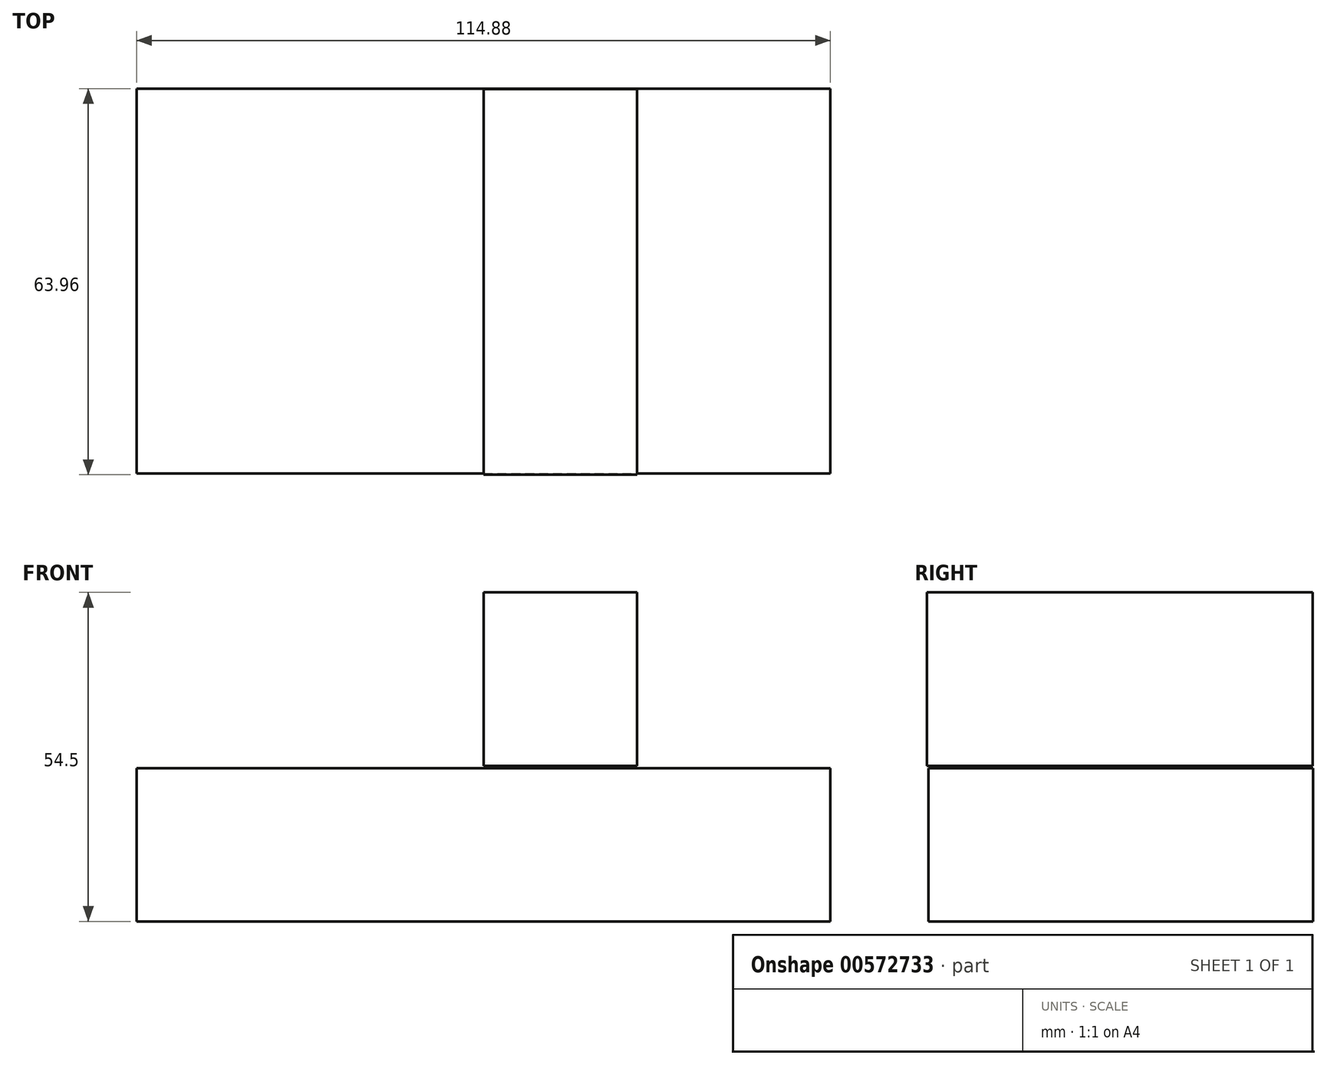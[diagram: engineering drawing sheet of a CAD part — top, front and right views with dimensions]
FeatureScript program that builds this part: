
annotation { "Feature Type Name" : "Feature", "Feature Type Description" : "" }
export const myFeature = defineFeature(function(context is Context, id is Id, definition is map)
    precondition{}
    {
        {
            var Q0;
            Q0=qCreatedBy(makeId("Top.planeOp"),FACE);
            var sketch = newSketch(context, id + "F0", { "sketchPlane" : qUnion([Q0])});
            skLineSegment(sketch, "E0.bottom", {"start": v(-57.44, -31.87) * mm, "end": v(57.44, -31.87) * mm});
            skLineSegment(sketch, "E0.top", {"start": v(-57.44, 31.87) * mm, "end": v(57.44, 31.87) * mm});
            skLineSegment(sketch, "E0.left", {"start": v(-57.44, -31.87) * mm, "end": v(-57.44, 31.87) * mm});
            skLineSegment(sketch, "E0.right", {"start": v(57.44, -31.87) * mm, "end": v(57.44, 31.87) * mm});
            skPoint(sketch, "E0.middle", {"position": v(0, 0) * mm});
            skSolve(sketch);
        }
        {
            var Q0;
            Q0 = qSketchRegion(id + "F0", true);
            extrude(context, id + "F1", {"entities" : qUnion([Q0]), "depth" : 25.4 * mm, "offsetDistance" : 25.4 * mm});
        }
        {
            var Q0;
            Q0=qCreatedBy(makeId("Right.planeOp"),FACE);
            var sketch = newSketch(context, id + "F2", { "sketchPlane" : qUnion([Q0])});
            skLineSegment(sketch, "E1.bottom", {"start": v(31.8, 54.5) * mm, "end": v(-32.09, 54.5) * mm});
            skLineSegment(sketch, "E1.top", {"start": v(31.8, 25.78) * mm, "end": v(-32.09, 25.78) * mm});
            skLineSegment(sketch, "E1.left", {"start": v(31.8, 54.5) * mm, "end": v(31.8, 25.78) * mm});
            skLineSegment(sketch, "E1.right", {"start": v(-32.09, 54.5) * mm, "end": v(-32.09, 25.78) * mm});
            skSolve(sketch);
        }
        {
            var Q0;
            Q0 = qSketchRegion(id + "F2", true);
            extrude(context, id + "F3", {"entities" : qUnion([Q0]), "depth" : 25.4 * mm, "offsetDistance" : 25.4 * mm});
        }
    });
